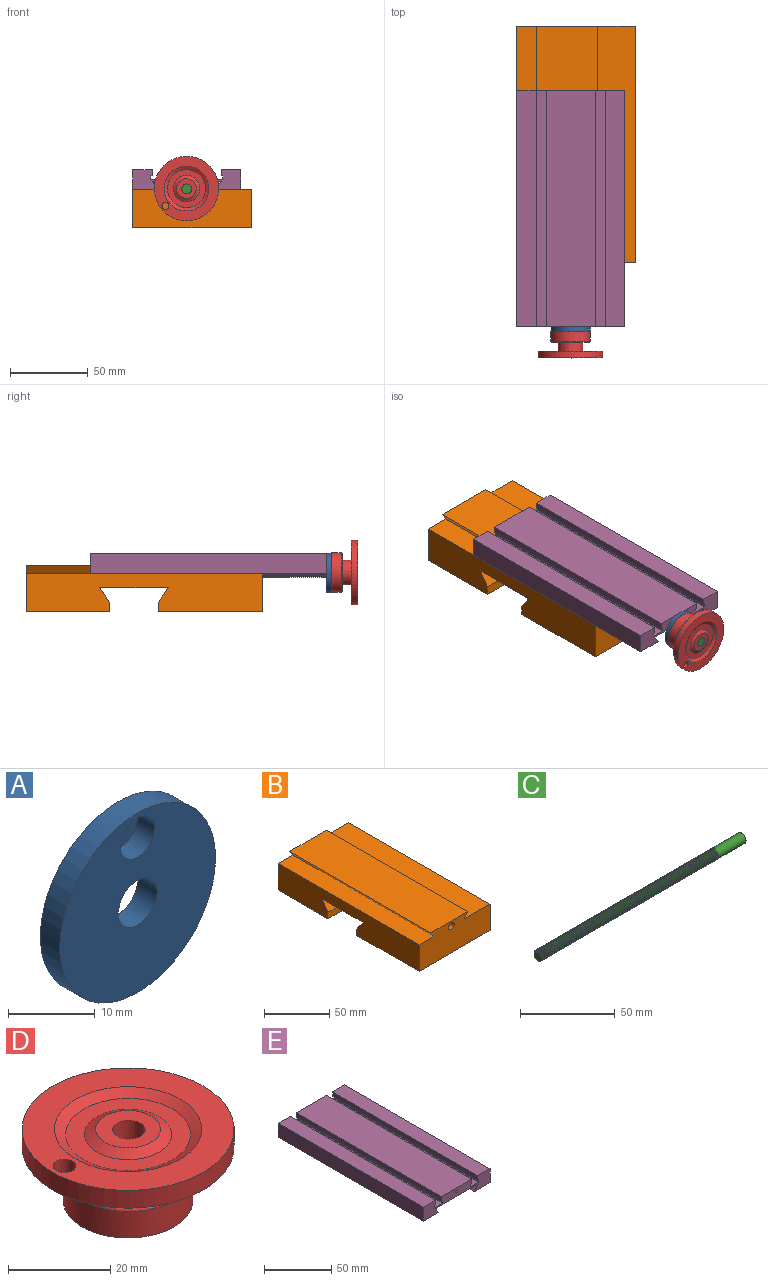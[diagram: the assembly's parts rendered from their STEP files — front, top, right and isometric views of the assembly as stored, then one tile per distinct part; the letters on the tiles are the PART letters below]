
ASSEMBLY  parts=5 mates=6
PART A: 7 faces, bbox 25.4x3.2x25.4 mm
  f0: cylinder r=12.7mm len=25.4mm, axis (0,1,0), area 253.4mm2, adj f1,f2
  f1: plane 25.4x25.4mm, normal (0,-1,0), area 450.8mm2, adj f0,f3,f6
  f2: plane 25.4x25.4mm, normal (0,1,0), area 471mm2, adj f0,f3,f4
  f3: cylinder r=3.17mm len=6.35mm, axis (0,-1,0), area 63.3mm2, adj f1,f2
  f4: cylinder r=1.13mm len=2.26mm, axis (0,-1,0), area 2.3mm2, adj f2,f5
  f5: plane 5.56x5.56mm, normal (0,-1,0), area 20.2mm2, adj f4,f6
  f6: cylinder r=2.78mm len=5.56mm, axis (0,-1,0), area 49.7mm2, adj f1,f5
PART B: 17 faces, bbox 76.6x152.4x29.8 mm
  f0: plane 152.4x24.68mm, normal (-1,0,0), area 3211.4mm2, adj f1,f2,f6,f9,f10,f11,f12,f13
  f1: plane 76.63x67.09mm, normal (0,0,-1), area 5141.4mm2, adj f0,f3,f9,f14
  f2: plane 76.63x53.95mm, normal (0,0,-1), area 4134.3mm2, adj f0,f3,f10,f15
  f3: plane 152.4x24.68mm, normal (1,0,0), area 3211.4mm2, adj f1,f2,f7,f9,f10,f11,f12,f13
  f4: plane 152.4x39.72mm, normal (0,0,1), area 6053.6mm2, adj f5,f8,f9,f10
  f5: plane 152.4x5.08mm, normal (-0.82,0,-0.57), area 939.4mm2, adj f4,f6,f9,f10
  f6: plane 152.4x16.19mm, normal (0,0,1), area 2467.6mm2, adj f0,f5,f9,f10
  f7: plane 152.4x27.7mm, normal (0,0,1), area 4221.7mm2, adj f3,f8,f9,f10
  f8: plane 152.4x5.08mm, normal (0.82,0,-0.57), area 939.4mm2, adj f4,f7,f9,f10
  f9: plane 76.63x29.76mm, normal (0,-1,0), area 2043.5mm2, adj f0,f1,f3,f4,f5,f6,f7,f8
  f10: plane 76.63x29.76mm, normal (0,1,0), area 2043.5mm2, adj f0,f2,f3,f4,f5,f6,f7,f8
  f11: plane 76.63x9.53mm, normal (0,-0.82,0.57), area 885.7mm2, adj f0,f3,f12,f15
  f12: plane 76.63x44.45mm, normal (0,0,-1), area 3406.3mm2, adj f0,f3,f11,f13
  f13: plane 76.63x9.53mm, normal (0,0.82,0.57), area 885.7mm2, adj f0,f3,f12,f14
  f14: plane 76.63x6.01mm, normal (0,1,0), area 460.4mm2, adj f0,f1,f3,f13
  f15: plane 76.63x6.01mm, normal (0,-1,0), area 460.4mm2, adj f0,f2,f3,f11
  f16: cylinder r=3.17mm len=152.4mm, axis (0,-1,0), area 3040.2mm2, adj f9,f10
PART C: 111 faces, bbox 153.8x8x7 mm
  f0: plane 6.11x6.07mm, normal (-1,0,0), area 23.5mm2, adj f1,f106,f107,f108
  f1: cylinder r=3.17mm len=6.35mm, axis (-1,0,0), area 1.5mm2, adj f0,f2,f106,f108
  f2: cylinder r=3.17mm len=6.35mm, axis (-1,0,0), area 2.1mm2, adj f1,f3,f106,f108
  f3: cylinder r=3.17mm len=6.35mm, axis (-1,0,0), area 2.1mm2, adj f2,f4,f106,f108
  f4: cylinder r=3.17mm len=6.35mm, axis (-1,0,0), area 2.1mm2, adj f3,f5,f106,f108
  f5: cylinder r=3.17mm len=6.35mm, axis (-1,0,0), area 2.1mm2, adj f4,f6,f106,f108
  f6: cylinder r=3.17mm len=6.35mm, axis (-1,0,0), area 2.1mm2, adj f5,f7,f106,f108
  f7: cylinder r=3.17mm len=6.35mm, axis (-1,0,0), area 2.1mm2, adj f6,f8,f106,f108
  f8: cylinder r=3.17mm len=6.35mm, axis (-1,0,0), area 2.1mm2, adj f7,f9,f106,f108
  f9: cylinder r=3.17mm len=6.35mm, axis (-1,0,0), area 2.1mm2, adj f8,f10,f106,f108
  f10: cylinder r=3.17mm len=6.35mm, axis (-1,0,0), area 2.1mm2, adj f9,f11,f106,f108
  f11: cylinder r=3.17mm len=6.35mm, axis (-1,0,0), area 2.1mm2, adj f10,f12,f106,f108
  f12: cylinder r=3.17mm len=6.35mm, axis (-1,0,0), area 2.1mm2, adj f11,f13,f106,f108
  f13: cylinder r=3.17mm len=6.35mm, axis (-1,0,0), area 2.1mm2, adj f12,f14,f106,f108
  f14: cylinder r=3.17mm len=6.35mm, axis (-1,0,0), area 2.1mm2, adj f13,f15,f106,f108
  f15: cylinder r=3.17mm len=6.35mm, axis (-1,0,0), area 2.1mm2, adj f14,f16,f106,f108
  f16: cylinder r=3.17mm len=6.35mm, axis (-1,0,0), area 2.1mm2, adj f15,f17,f106,f108
  f17: cylinder r=3.17mm len=6.35mm, axis (-1,0,0), area 2.1mm2, adj f16,f18,f106,f108
  f18: cylinder r=3.17mm len=6.35mm, axis (-1,0,0), area 2.1mm2, adj f17,f19,f106,f108
  f19: cylinder r=3.17mm len=6.35mm, axis (-1,0,0), area 2.1mm2, adj f18,f20,f106,f108
  f20: cylinder r=3.17mm len=6.35mm, axis (-1,0,0), area 2.1mm2, adj f19,f21,f106,f108
  f21: cylinder r=3.17mm len=6.35mm, axis (-1,0,0), area 2.1mm2, adj f20,f22,f106,f108
  f22: cylinder r=3.17mm len=6.35mm, axis (-1,0,0), area 2.1mm2, adj f21,f23,f106,f108
  f23: cylinder r=3.17mm len=6.35mm, axis (-1,0,0), area 2.1mm2, adj f22,f24,f106,f108
  f24: cylinder r=3.17mm len=6.35mm, axis (-1,0,0), area 2.1mm2, adj f23,f25,f106,f108
  f25: cylinder r=3.17mm len=6.35mm, axis (-1,0,0), area 2.1mm2, adj f24,f26,f106,f108
  f26: cylinder r=3.17mm len=6.35mm, axis (-1,0,0), area 2.1mm2, adj f25,f27,f106,f108
  f27: cylinder r=3.17mm len=6.35mm, axis (-1,0,0), area 2.1mm2, adj f26,f28,f106,f108
  f28: cylinder r=3.17mm len=6.35mm, axis (-1,0,0), area 2.1mm2, adj f27,f29,f106,f108
  f29: cylinder r=3.17mm len=6.35mm, axis (-1,0,0), area 2.1mm2, adj f28,f30,f106,f108
  f30: cylinder r=3.17mm len=6.35mm, axis (-1,0,0), area 2.1mm2, adj f29,f31,f106,f108
  f31: cylinder r=3.17mm len=6.35mm, axis (-1,0,0), area 2.1mm2, adj f30,f32,f106,f108
  f32: cylinder r=3.17mm len=6.35mm, axis (-1,0,0), area 2.1mm2, adj f31,f33,f106,f108
  f33: cylinder r=3.17mm len=6.35mm, axis (-1,0,0), area 2.1mm2, adj f32,f34,f106,f108
  f34: cylinder r=3.17mm len=6.35mm, axis (-1,0,0), area 2.1mm2, adj f33,f35,f106,f108
  f35: cylinder r=3.17mm len=6.35mm, axis (-1,0,0), area 2.1mm2, adj f34,f36,f106,f108
  f36: cylinder r=3.17mm len=6.35mm, axis (-1,0,0), area 2.1mm2, adj f35,f37,f106,f108
  f37: cylinder r=3.17mm len=6.35mm, axis (-1,0,0), area 2.1mm2, adj f36,f38,f106,f108
  f38: cylinder r=3.17mm len=6.35mm, axis (-1,0,0), area 2.1mm2, adj f37,f39,f106,f108
  f39: cylinder r=3.17mm len=6.35mm, axis (-1,0,0), area 2.1mm2, adj f38,f40,f106,f108
  f40: cylinder r=3.17mm len=6.35mm, axis (-1,0,0), area 2.1mm2, adj f39,f41,f106,f108
  f41: cylinder r=3.17mm len=6.35mm, axis (-1,0,0), area 2.1mm2, adj f40,f42,f106,f108
  f42: cylinder r=3.17mm len=6.35mm, axis (-1,0,0), area 2.1mm2, adj f41,f43,f106,f108
  f43: cylinder r=3.17mm len=6.35mm, axis (-1,0,0), area 2.1mm2, adj f42,f44,f106,f108
  f44: cylinder r=3.17mm len=6.35mm, axis (-1,0,0), area 2.1mm2, adj f43,f45,f106,f108
  f45: cylinder r=3.17mm len=6.35mm, axis (-1,0,0), area 2.1mm2, adj f44,f46,f106,f108
  f46: cylinder r=3.17mm len=6.35mm, axis (-1,0,0), area 2.1mm2, adj f45,f47,f106,f108
  f47: cylinder r=3.17mm len=6.35mm, axis (-1,0,0), area 2.1mm2, adj f46,f48,f106,f108
  f48: cylinder r=3.17mm len=6.35mm, axis (-1,0,0), area 2.1mm2, adj f47,f49,f106,f108
  f49: cylinder r=3.17mm len=6.35mm, axis (-1,0,0), area 2.1mm2, adj f48,f50,f106,f108
  f50: cylinder r=3.17mm len=6.35mm, axis (-1,0,0), area 2.1mm2, adj f49,f51,f106,f108
  f51: cylinder r=3.17mm len=6.35mm, axis (-1,0,0), area 2.1mm2, adj f50,f52,f106,f108
  f52: cylinder r=3.17mm len=6.35mm, axis (-1,0,0), area 2.1mm2, adj f51,f53,f106,f108
  f53: cylinder r=3.17mm len=6.35mm, axis (-1,0,0), area 2.1mm2, adj f52,f54,f106,f108
  f54: cylinder r=3.17mm len=6.35mm, axis (-1,0,0), area 2.1mm2, adj f53,f55,f106,f108
  f55: cylinder r=3.17mm len=6.35mm, axis (-1,0,0), area 2.1mm2, adj f54,f56,f106,f108
  f56: cylinder r=3.17mm len=6.35mm, axis (-1,0,0), area 2.1mm2, adj f55,f57,f106,f108
  f57: cylinder r=3.17mm len=6.35mm, axis (-1,0,0), area 2.1mm2, adj f56,f58,f106,f108
  f58: cylinder r=3.17mm len=6.35mm, axis (-1,0,0), area 2.1mm2, adj f57,f59,f106,f108
  f59: cylinder r=3.17mm len=6.35mm, axis (-1,0,0), area 2.1mm2, adj f58,f60,f106,f108
  f60: cylinder r=3.17mm len=6.35mm, axis (-1,0,0), area 2.1mm2, adj f59,f61,f106,f108
  f61: cylinder r=3.17mm len=6.35mm, axis (-1,0,0), area 2.1mm2, adj f60,f62,f106,f108
  f62: cylinder r=3.17mm len=6.35mm, axis (-1,0,0), area 2.1mm2, adj f61,f63,f106,f108
  f63: cylinder r=3.17mm len=6.35mm, axis (-1,0,0), area 2.1mm2, adj f62,f64,f106,f108
  f64: cylinder r=3.17mm len=6.35mm, axis (-1,0,0), area 2.1mm2, adj f63,f65,f106,f108
  f65: cylinder r=3.17mm len=6.35mm, axis (-1,0,0), area 2.1mm2, adj f64,f66,f106,f108
  f66: cylinder r=3.17mm len=6.35mm, axis (-1,0,0), area 2.1mm2, adj f65,f67,f106,f108
  f67: cylinder r=3.17mm len=6.35mm, axis (-1,0,0), area 2.1mm2, adj f66,f68,f106,f108
  f68: cylinder r=3.17mm len=6.35mm, axis (-1,0,0), area 2.1mm2, adj f67,f69,f106,f108
  f69: cylinder r=3.17mm len=6.35mm, axis (-1,0,0), area 2.1mm2, adj f68,f70,f106,f108
  f70: cylinder r=3.17mm len=6.35mm, axis (-1,0,0), area 2.1mm2, adj f69,f71,f106,f108
  f71: cylinder r=3.17mm len=6.35mm, axis (-1,0,0), area 2.1mm2, adj f70,f72,f106,f108
  f72: cylinder r=3.17mm len=6.35mm, axis (-1,0,0), area 2.1mm2, adj f71,f73,f106,f108
  f73: cylinder r=3.17mm len=6.35mm, axis (-1,0,0), area 2.1mm2, adj f72,f74,f106,f108
  f74: cylinder r=3.17mm len=6.35mm, axis (-1,0,0), area 2.1mm2, adj f73,f75,f106,f108
  f75: cylinder r=3.17mm len=6.35mm, axis (-1,0,0), area 2.1mm2, adj f74,f76,f106,f108
  f76: cylinder r=3.17mm len=6.35mm, axis (-1,0,0), area 2.1mm2, adj f75,f77,f106,f108
  f77: cylinder r=3.17mm len=6.35mm, axis (-1,0,0), area 2.1mm2, adj f76,f78,f106,f108
  f78: cylinder r=3.17mm len=6.35mm, axis (-1,0,0), area 2.1mm2, adj f77,f79,f106,f108
  f79: cylinder r=3.17mm len=6.35mm, axis (-1,0,0), area 2.1mm2, adj f78,f80,f106,f108
  f80: cylinder r=3.17mm len=6.35mm, axis (-1,0,0), area 2.1mm2, adj f79,f81,f106,f108
  f81: cylinder r=3.17mm len=6.35mm, axis (-1,0,0), area 2.1mm2, adj f80,f82,f106,f108
  f82: cylinder r=3.17mm len=6.35mm, axis (-1,0,0), area 2.1mm2, adj f81,f83,f106,f108
  f83: cylinder r=3.17mm len=6.35mm, axis (-1,0,0), area 2.1mm2, adj f82,f84,f106,f108
  f84: cylinder r=3.17mm len=6.35mm, axis (-1,0,0), area 2.1mm2, adj f83,f85,f106,f108
  f85: cylinder r=3.17mm len=6.35mm, axis (-1,0,0), area 2.1mm2, adj f84,f86,f106,f108
  f86: cylinder r=3.17mm len=6.35mm, axis (-1,0,0), area 2.1mm2, adj f85,f87,f106,f108
  f87: cylinder r=3.17mm len=6.35mm, axis (-1,0,0), area 2.1mm2, adj f86,f88,f106,f108
  f88: cylinder r=3.17mm len=6.35mm, axis (-1,0,0), area 2.1mm2, adj f87,f89,f106,f108
  f89: cylinder r=3.17mm len=6.35mm, axis (-1,0,0), area 2.1mm2, adj f88,f90,f106,f108
  f90: cylinder r=3.17mm len=6.35mm, axis (-1,0,0), area 2.1mm2, adj f89,f91,f106,f108
  f91: cylinder r=3.17mm len=6.35mm, axis (-1,0,0), area 2.1mm2, adj f90,f92,f106,f108
  f92: cylinder r=3.17mm len=6.35mm, axis (-1,0,0), area 2.1mm2, adj f91,f93,f106,f108
  f93: cylinder r=3.17mm len=6.35mm, axis (-1,0,0), area 2.1mm2, adj f92,f94,f106,f108
  f94: cylinder r=3.17mm len=6.35mm, axis (-1,0,0), area 2.1mm2, adj f93,f95,f106,f108
  f95: cylinder r=3.17mm len=6.35mm, axis (-1,0,0), area 2.1mm2, adj f94,f96,f106,f108
  f96: cylinder r=3.17mm len=6.35mm, axis (-1,0,0), area 2.1mm2, adj f95,f97,f106,f108
  f97: cylinder r=3.17mm len=6.35mm, axis (-1,0,0), area 2.1mm2, adj f96,f98,f106,f108
  f98: cylinder r=3.17mm len=6.35mm, axis (-1,0,0), area 2.1mm2, adj f97,f99,f106,f108
  f99: cylinder r=3.17mm len=6.35mm, axis (-1,0,0), area 2.1mm2, adj f98,f100,f106,f108
  f100: cylinder r=3.17mm len=6.35mm, axis (-1,0,0), area 2.1mm2, adj f99,f101,f106,f108
  f101: cylinder r=3.17mm len=6.35mm, axis (-1,0,0), area 2.1mm2, adj f100,f102,f106,f108
  f102: cylinder r=3.17mm len=6.35mm, axis (-1,0,0), area 2.1mm2, adj f101,f103,f106,f108
  f103: cylinder r=3.17mm len=6.35mm, axis (-1,0,0), area 2.1mm2, adj f102,f104,f106,f108
  f104: cylinder r=3.17mm len=6.35mm, axis (-1,0,0), area 2.1mm2, adj f103,f105,f106,f108
  f105: cylinder r=3.17mm len=20.72mm, axis (-1,0,0), area 400.8mm2, adj f104,f106,f109,f110
  f106: bspline ~133.67x7.33mm, area 1894.6mm2, adj f0,f1,f2,f3,f4,f5,f6,f7
  f107: cylinder r=2.26mm len=132.42mm, axis (1,0,0), area 1236.6mm2, adj f0,f106,f108,f109
  f108: bspline ~133.03x7.33mm, area 1887mm2, adj f0,f1,f2,f3,f4,f5,f6,f7
  f109: plane 1.17x0.92mm, normal (0,1,0), area 0.6mm2, adj f105,f106,f107,f108
  f110: plane 6.35x6.35mm, normal (1,0,0), area 31.7mm2, adj f105
PART D: 14 faces, bbox 41.6x41.6x17.1 mm
  f0: plane 25.4x25.4mm, normal (0,0,-1), area 475mm2, adj f10,f12
  f1: plane 12.7x12.7mm, normal (0,0,1), area 95mm2, adj f2,f12
  f2: cone r=8.55mm half-angle=60deg, axis (0,0,-1), area 118.9mm2, adj f1,f3
  f3: plane 24.49x24.49mm, normal (0,0,1), area 241.5mm2, adj f2,f4
  f4: cone r=14.45mm half-angle=60deg, axis (0,0,1), area 213mm2, adj f3,f5
  f5: plane 41.59x41.59mm, normal (0,0,1), area 687.5mm2, adj f4,f6,f13
  f6: cylinder r=20.8mm len=41.59mm, axis (0,0,1), area 555.9mm2, adj f5,f7
  f7: plane 41.59x41.59mm, normal (0,0,-1), area 1145.2mm2, adj f6,f8,f13
  f8: cylinder r=7.94mm len=15.88mm, axis (0,0,1), area 294.5mm2, adj f7,f9
  f9: plane 24.13x24.13mm, normal (0,0,1), area 259.4mm2, adj f8,f11
  f10: cylinder r=12.7mm len=25.4mm, axis (0,0,1), area 506.7mm2, adj f0,f11
  f11: torus R=12.06mm, axis (0,0,-1), area 78.1mm2, adj f9,f10
  f12: cylinder r=3.17mm len=17.15mm, axis (0,0,1), area 342mm2, adj f0,f1
  f13: cylinder r=2.22mm len=4.45mm, axis (0,0,1), area 59.4mm2, adj f5,f7
PART E: 28 faces, bbox 69.9x152.4x12.7 mm
  f0: plane 152.4x12.7mm, normal (0,0,1), area 1935.5mm2, adj f2,f3,f11,f25
  f1: plane 152.4x31.75mm, normal (0,0,1), area 4838.7mm2, adj f2,f3,f18,f19
  f2: plane 69.85x12.7mm, normal (0,-1,0), area 583.9mm2, adj f0,f1,f4,f5,f6,f7,f8,f9
  f3: plane 69.85x12.7mm, normal (0,1,0), area 587.9mm2, adj f0,f1,f4,f5,f6,f7,f8,f9
  f4: plane 152.4x12.7mm, normal (0,0,1), area 1935.5mm2, adj f2,f3,f5,f12
  f5: plane 152.4x12.7mm, normal (-1,0,0), area 1935.5mm2, adj f2,f3,f4,f6
  f6: plane 152.4x16.19mm, normal (0,0,-1), area 2467.6mm2, adj f2,f3,f5,f7
  f7: plane 152.4x5.08mm, normal (0.82,0,0.57), area 939.4mm2, adj f2,f3,f6,f8
  f8: plane 152.4x44.45mm, normal (0,0,-1), area 6774.2mm2, adj f2,f3,f7,f9
  f9: plane 152.4x5.08mm, normal (-0.82,0,0.57), area 939.4mm2, adj f2,f3,f8,f10
  f10: plane 152.4x16.19mm, normal (0,0,-1), area 2467.6mm2, adj f2,f3,f9,f11
  f11: plane 152.4x12.7mm, normal (1,0,0), area 1935.5mm2, adj f0,f2,f3,f10
  f12: plane 152.4x4.06mm, normal (1,0,0), area 619.4mm2, adj f2,f3,f4,f13
  f13: plane 152.4x1.14mm, normal (0,0,-1), area 174.2mm2, adj f2,f3,f12,f14
  f14: plane 152.4x2.29mm, normal (1,0,0), area 348.4mm2, adj f2,f3,f13,f15
  f15: plane 152.4x8.64mm, normal (0,0,1), area 1316.1mm2, adj f2,f3,f14,f16
  f16: plane 152.4x2.29mm, normal (-1,0,0), area 348.4mm2, adj f2,f3,f15,f17
  f17: plane 152.4x1.14mm, normal (0,0,-1), area 174.2mm2, adj f2,f3,f16,f18
  f18: plane 152.4x4.06mm, normal (-1,0,0), area 619.4mm2, adj f1,f2,f3,f17
  f19: plane 152.4x4.06mm, normal (1,0,0), area 619.4mm2, adj f1,f2,f3,f20
  f20: plane 152.4x1.14mm, normal (0,0,-1), area 174.2mm2, adj f2,f3,f19,f21
  f21: plane 152.4x2.29mm, normal (1,0,0), area 348.4mm2, adj f2,f3,f20,f22
  f22: plane 152.4x8.64mm, normal (0,0,1), area 1316.1mm2, adj f2,f3,f21,f23
  f23: plane 152.4x2.29mm, normal (-1,0,0), area 348.4mm2, adj f2,f3,f22,f24
  f24: plane 152.4x1.14mm, normal (0,0,-1), area 174.2mm2, adj f2,f3,f23,f25
  f25: plane 152.4x4.06mm, normal (-1,0,0), area 619.4mm2, adj f0,f2,f3,f24
  f26: cone r=0mm half-angle=59deg, axis (0,-1,0), area 4.7mm2, adj f27
  f27: cylinder r=1.13mm len=12.7mm, axis (0,-1,0), area 90.2mm2, adj f2,f26
PLACE A rot(axis=(0,-1,-0.01),0deg) t=(-196.78,34.81,-40.3)mm
PLACE B t=(-196.78,76.2,-40.3)mm
PLACE C rot(axis=(-0.39,0.39,-0.83),100.6deg) t=(-34.37,51.94,-0.35)mm
PLACE D rot(axis=(0.89,-0.32,0.32),96.5deg) t=(-3.55,-44.57,25.19)mm
PLACE E rot(axis=(0.01,-1,0),0deg) t=(-196.78,34.81,-40.3)mm
MATE planar E.f8 <-> B.f4  axis (0,0,-1) through (-3.39,34.81,29.76)mm
MATE fastened D.f12 <-> C.f1  axis (0,-1,0) through (-3.39,-61.71,24.99)mm
MATE fastened E.f26 <-> A.f4  axis (0,-1,0) through (-3.39,-41.39,34.2)mm
MATE cylindrical C.f1 <-> A.f0  axis (0,-1,0) through (-3.39,-61.71,24.99)mm
MATE planar A.f1 <-> D.f0  axis (0,-1,0) through (-3.39,-44.57,24.5)mm
MATE cylindrical C.f1 <-> B.f16  axis (0,-1,0) through (-3.39,90.69,24.99)mm
